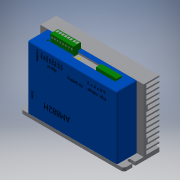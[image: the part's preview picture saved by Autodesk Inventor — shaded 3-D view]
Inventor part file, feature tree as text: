
AUTODESK INVENTOR PART (.ipt)
format: ipt  version: 2016 (Build 200138000, 138)  size: 552,448 bytes
history: native  units: mm
features: sketch x16, extrude x15, fillet x2
ambient origin geometry x8: Origin, YZ Plane, XZ Plane, XY Plane, X Axis, Y Axis, Z Axis, Center Point
bodies: Solid1 (feature_tree)
feature tree (33):
  extrude  "Extrusion1"  Depth=75.5mm
  extrude  "Extrusion2"  Depth=4.5mm
  extrude  "Extrusion3"  Depth=69.5mm
  extrude  "Extrusion4"  Depth=5.0mm TaperAngle=0.0deg
  fillet  "Fillet3"  Radius=14.5mm
  extrude  "Extrusion5"  Depth=10.0mm
  extrude  "Extrusion7"  Depth=0.1mm TaperAngle=0.0deg
  extrude  "Extrusion8"  Depth=2.0mm
  extrude  "Extrusion9"  Depth=5.0mm
  extrude  "Extrusion10"  Depth=5.0mm
  extrude  "Extrusion11"  Depth=5.0mm
  extrude  "Extrusion12"  Depth=5.0mm
  fillet  "Fillet4"  Radius=2.0mm
  extrude  "Extrusion13"  Depth=2.0mm
  extrude  "Extrusion14"  Depth=2.0mm
  extrude  "Extrusion15"  Depth=2.0mm
  extrude  "Extrusion16"  Depth=2.0mm
  sketch  "Sketch16"  dims[d47=5.0mm d48=2.0mm d49=5.0mm d50=2.0mm d51=5.0mm d52=2.0mm d53=5.0mm d54=2.0mm d55=5.0mm d56=6.0mm d57=6.0mm d58=10.0mm d59=0.0mm d66=46.0mm d67=50.0mm d68=16.0mm d69=0.0mm d70=50.0mm d71=50.0mm d72=18.5mm d73=49.0mm d74=14.0mm d75=0.0mm d76=13.0mm d77=13.0mm d78=20.0mm d79=5.0mm d80=0.25mm d81=0.0mm d82=3.0mm d83=3.0mm d84=8.0mm d85=14.0mm d86=7.0mm d87=7.0mm d88=18.5mm d89=15.0mm d90=15.0mm d91=34.0mm d92=10.0mm d93=64.0mm d94=6.0mm d95=6.0mm d96=2.5mm d97=0.0mm d98=8.0mm d99=30.0mm d100=5.0mm d101=0.0mm d102=25.0mm d103=25.0mm d104=41.0mm d105=2.0mm d106=4.0mm d107=2.0mm d108=4.0mm d109=2.0mm d110=2.0mm d111=0.0mm d112=1.0mm d116=8.0mm d117=0.0mm d118=0.25mm d120=11.0mm d121=1.0mm d122=1.0mm d123=3.0mm d124=4.0mm d125=3.0mm d126=3.0mm d127=3.0mm d128=3.0mm d129=3.0mm d130=3.0mm d131=3.0mm d132=1.0mm d133=1.0mm d134=1.75mm d135=1.0mm d136=1.0mm d137=1.0mm d138=1.0mm d139=1.0mm d140=0.25mm d141=0.0mm d142=2.5mm d143=2.5mm d144=2.5mm d145=1.5mm d146=1.5mm d147=1.5mm d148=2.5mm d149=2.5mm d150=2.5mm d151=2.5mm d152=2.5mm d153=1.5mm d154=1.5mm d155=1.5mm d156=1.5mm d157=1.5mm d158=0.25mm d159=0.0mm d160=4.0mm d161=4.0mm d162=4.0mm d163=4.0mm d164=4.0mm d165=4.0mm d166=4.0mm d167=4.0mm d168=4.0mm d169=5.0mm d170=6.0mm d171=0.25mm d172=0.0mm]
  sketch  "Sketch1"  dims[d1=14.5mm d2=75.5mm d3=75.5mm d4=52.0mm]
  sketch  "Sketch2"  dims[d6=4.5mm d7=4.5mm]
  sketch  "Sketch3"  dims[d8=69.5mm d9=69.5mm]
  sketch  "Sketch4"  dims[d10=4.0mm d11=5.0mm d12=0.0mm d13=14.5mm]
  sketch  "Sketch5"  dims[d14=14.5mm d15=10.0mm d16=10.0mm]
  sketch  "Sketch6"  dims[d17=92.0mm d18=0.0mm d20=0.1mm d21=0.0mm]
  sketch  "Sketch7"  dims[d23=0.1mm d24=0.0mm d25=2.0mm]
  sketch  "Sketch8"  dims[d30=2.0mm d31=5.0mm]
  sketch  "Sketch9"  dims[d32=2.0mm d33=5.0mm]
  sketch  "Sketch10"  dims[d34=2.0mm d35=5.0mm]
  sketch  "Sketch11"  dims[d36=2.0mm d37=5.0mm d38=2.0mm]
  sketch  "Sketch12"  dims[d39=5.0mm d40=2.0mm]
  sketch  "Sketch13"  dims[d41=5.0mm d42=2.0mm]
  sketch  "Sketch14"  dims[d43=5.0mm d44=2.0mm]
  sketch  "Sketch15"  dims[d45=5.0mm d46=2.0mm]
